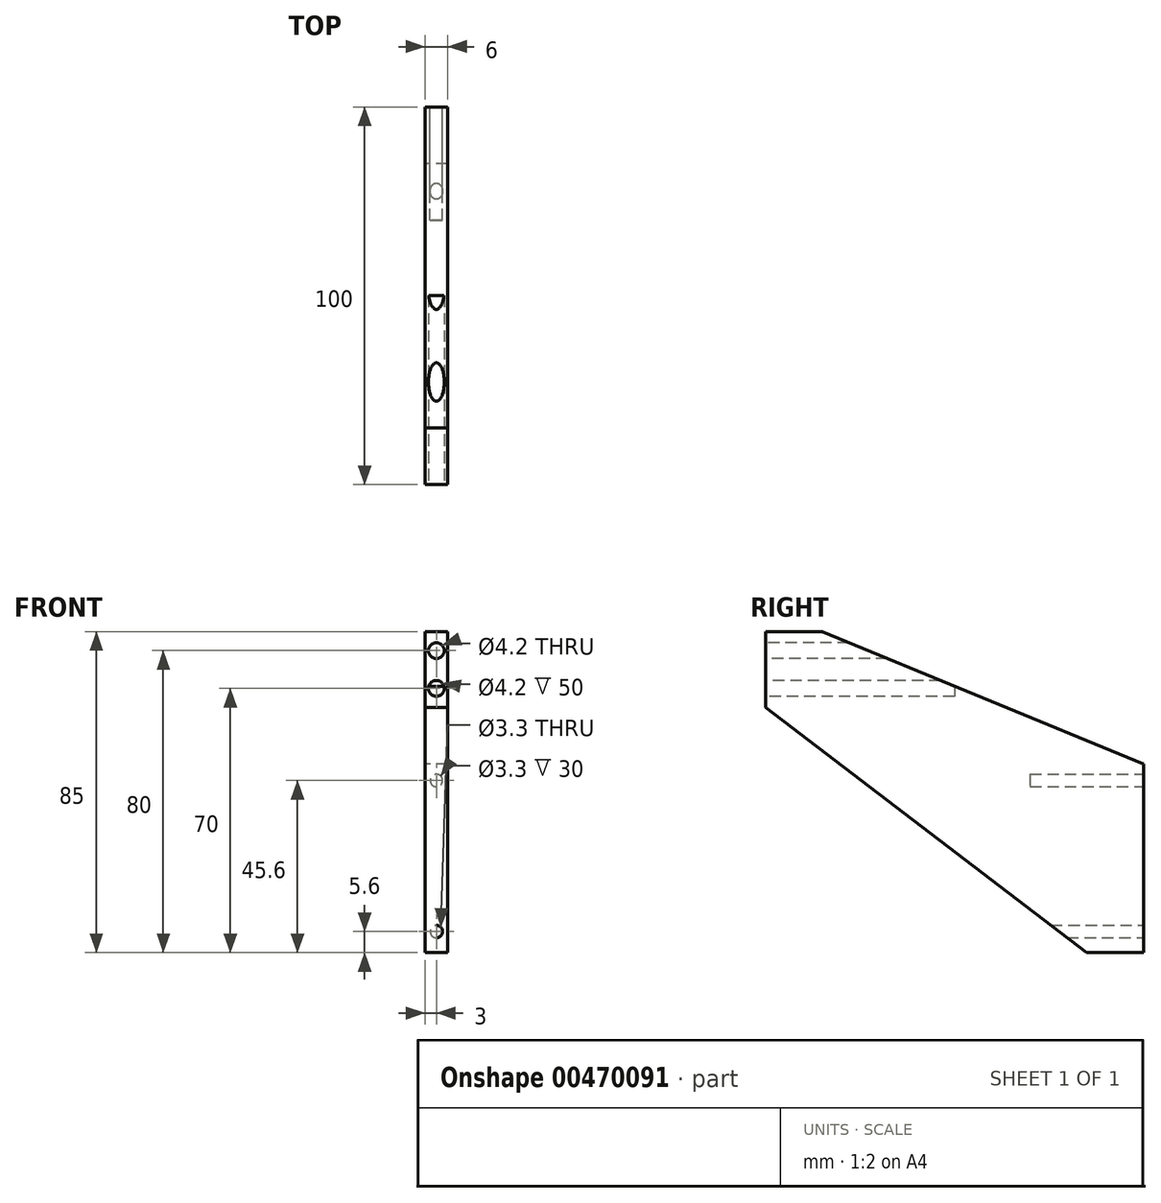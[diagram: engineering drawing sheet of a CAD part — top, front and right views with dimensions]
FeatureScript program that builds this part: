
annotation { "Feature Type Name" : "Feature", "Feature Type Description" : "" }
export const myFeature = defineFeature(function(context is Context, id is Id, definition is map)
    precondition{}
    {
        {
            var Q0;
            Q0=qCreatedBy(makeId("Right.planeOp"),FACE);
            var sketch = newSketch(context, id + "F0", { "sketchPlane" : qUnion([Q0])});
            skLineSegment(sketch, "E0", {"start": v(0, 0) * mm, "end": v(0, 50) * mm});
            skLineSegment(sketch, "E1", {"start": v(0, 0) * mm, "end": v(0, 0) * mm});
            skLineSegment(sketch, "E2", {"start": v(-100, 65) * mm, "end": v(-100, 85) * mm});
            skLineSegment(sketch, "E3", {"start": v(-100, 85) * mm, "end": v(-85, 85) * mm});
            skLineSegment(sketch, "E4", {"start": v(-85, 85) * mm, "end": v(0, 50) * mm});
            skLineSegment(sketch, "E5", {"start": v(0, 0) * mm, "end": v(-15, 0) * mm});
            skLineSegment(sketch, "E6", {"start": v(-15, 0) * mm, "end": v(-100, 65) * mm});
            skSolve(sketch);
        }
        {
            var Q0;
            Q0=makeQuery(id+"F0.imprint","IMPRINT",FACE,{"disambiguationData":[TD([[makeQuery(id+"F0.imprint","IMPRINT",EDGE,{"derivedFrom":sQuery(id+"F0.wireOp",EDGE,"E0")}),1.0]])]});
            extrude(context, id + "F1", {"entities" : qUnion([Q0]), "depth" : 6 * mm});
        }
        {
            var Q0;
            Q0=makeQuery(id+"F1.opExtrude","SWEPT_FACE",FACE,{"disambiguationData":[OSD([sQuery(id+"F0.wireOp",EDGE,"E2")])]});
            var sketch = newSketch(context, id + "F2", { "sketchPlane" : qUnion([Q0])});
            skCircle(sketch, "E7", {"center": v(3, 70) * mm, "radius": 2.1 * mm});
            skCircle(sketch, "E8", {"center": v(3, 80) * mm, "radius": 2.1 * mm});
            skLineSegment(sketch, "E9", {"start": v(3, 65) * mm, "end": v(3, 85) * mm, "construction": true});
            skSolve(sketch);
        }
        {
            var Q0;
            Q0=makeQuery(id+"F2.imprint","IMPRINT",FACE,{"disambiguationData":[TD([[makeQuery(id+"F2.imprint","IMPRINT",EDGE,{"derivedFrom":sQuery(id+"F2.wireOp",EDGE,"E7")}),1.0]])]});
            var Q1;
            Q1=makeQuery(id+"F2.imprint","IMPRINT",FACE,{"disambiguationData":[TD([[makeQuery(id+"F2.imprint","IMPRINT",EDGE,{"derivedFrom":sQuery(id+"F2.wireOp",EDGE,"E8")}),1.0]])]});
            extrude(context, id + "F3", {"entities" : qUnion([Q0, Q1]), "operationType" : NewBodyOperationType.REMOVE, "oppositeDirection" : true, "depth" : 50 * mm});
        }
        {
            var Q0;
            Q0=makeQuery(id+"F1.opExtrude","SWEPT_FACE",FACE,{"disambiguationData":[OSD([sQuery(id+"F0.wireOp",EDGE,"E0")])]});
            var sketch = newSketch(context, id + "F4", { "sketchPlane" : qUnion([Q0])});
            skLineSegment(sketch, "E10", {"start": v(-3, 0) * mm, "end": v(-3, 0) * mm});
            skCircle(sketch, "E11", {"center": v(-3, 45.6) * mm, "radius": 1.65 * mm});
            skCircle(sketch, "E12", {"center": v(-3, 5.6) * mm, "radius": 1.65 * mm});
            skLineSegment(sketch, "E13", {"start": v(-3, 0) * mm, "end": v(-3, 23.2) * mm, "construction": true});
            skSolve(sketch);
        }
        {
            var Q0;
            Q0=makeQuery(id+"F4.imprint","IMPRINT",FACE,{"disambiguationData":[TD([[makeQuery(id+"F4.imprint","IMPRINT",EDGE,{"derivedFrom":sQuery(id+"F4.wireOp",EDGE,"E11")}),1.0]])]});
            var Q1;
            Q1=makeQuery(id+"F4.imprint","IMPRINT",FACE,{"disambiguationData":[TD([[makeQuery(id+"F4.imprint","IMPRINT",EDGE,{"derivedFrom":sQuery(id+"F4.wireOp",EDGE,"E12")}),1.0]])]});
            extrude(context, id + "F5", {"entities" : qUnion([Q0, Q1]), "operationType" : NewBodyOperationType.REMOVE, "oppositeDirection" : true, "depth" : 30 * mm});
        }
    });
